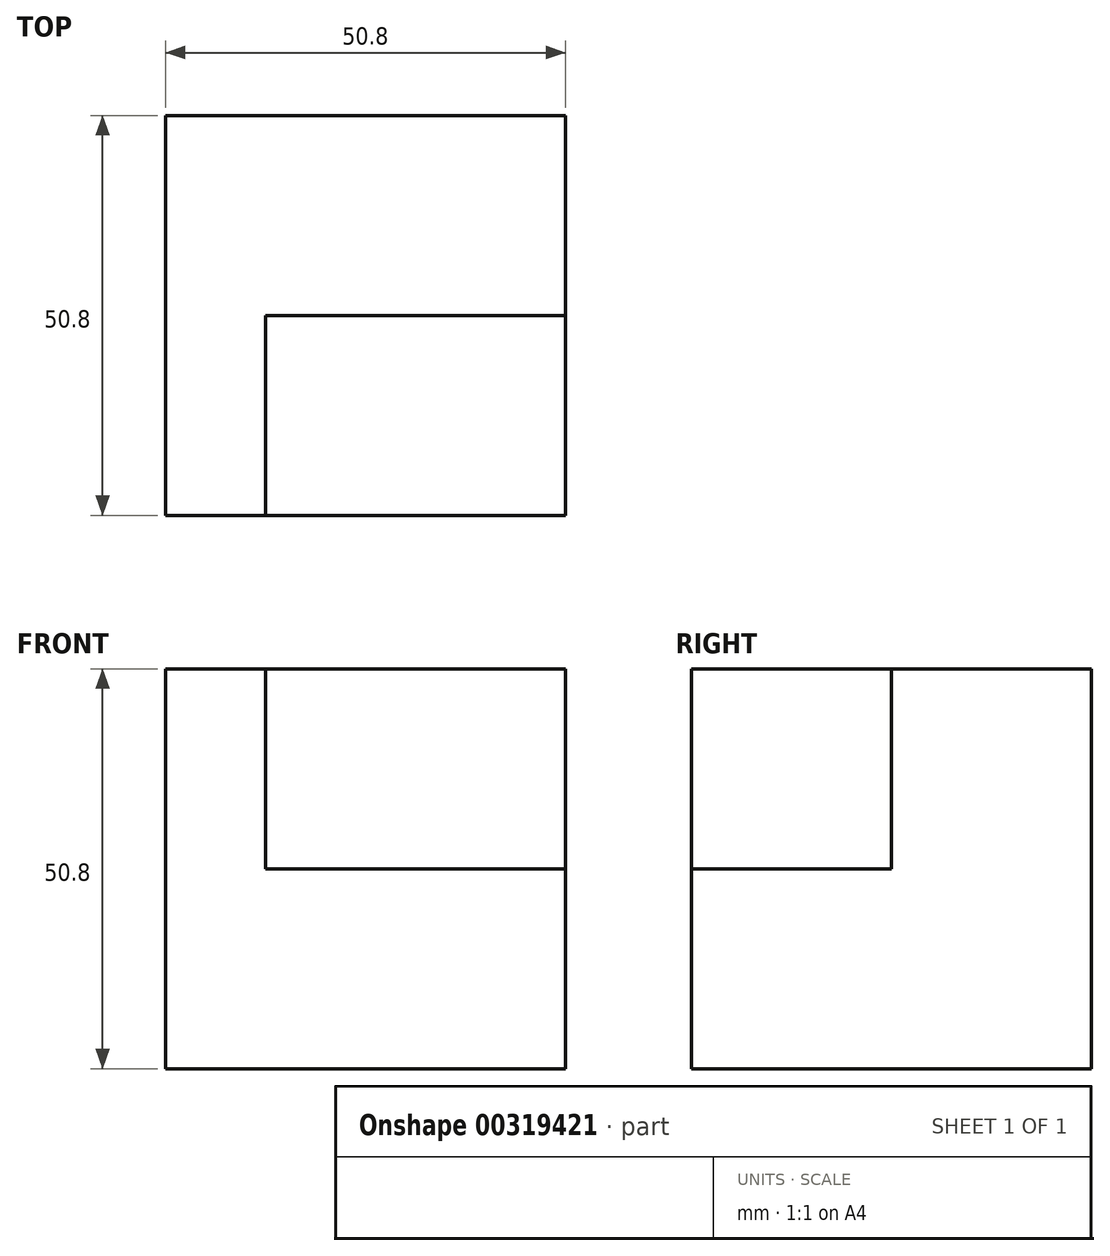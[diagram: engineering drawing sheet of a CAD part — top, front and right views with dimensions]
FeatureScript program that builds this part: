
annotation { "Feature Type Name" : "Feature", "Feature Type Description" : "" }
export const myFeature = defineFeature(function(context is Context, id is Id, definition is map)
    precondition{}
    {
        {
            var Q0;
            Q0=qCreatedBy(makeId("Top.planeOp"),FACE);
            var sketch = newSketch(context, id + "F0", { "sketchPlane" : qUnion([Q0])});
            skLineSegment(sketch, "E0", {"start": v(-38.83, -59.2) * mm, "end": v(11.97, -59.2) * mm});
            skLineSegment(sketch, "E1", {"start": v(11.97, -59.2) * mm, "end": v(11.97, -8.4) * mm});
            skLineSegment(sketch, "E2", {"start": v(11.97, -8.4) * mm, "end": v(-38.83, -8.4) * mm});
            skLineSegment(sketch, "E3", {"start": v(-38.83, -8.4) * mm, "end": v(-38.83, -59.2) * mm});
            skSolve(sketch);
        }
        {
            var Q0;
            Q0=makeQuery(id+"F0.imprint","IMPRINT",FACE,{"disambiguationData":[TD([[makeQuery(id+"F0.imprint","IMPRINT",EDGE,{"derivedFrom":sQuery(id+"F0.wireOp",EDGE,"E0")}),1.0]])]});
            extrude(context, id + "F1", {"entities" : qUnion([Q0]), "depth" : 25.4 * mm});
        }
        {
            var Q0;
            Q0=makeQuery(id+"F1.opExtrude","CAP_FACE",FACE,{"disambiguationData":[OSD([sQuery(id+"F0.wireOp",EDGE,"E0"),sQuery(id+"F0.wireOp",EDGE,"E1"),sQuery(id+"F0.wireOp",EDGE,"E2"),sQuery(id+"F0.wireOp",EDGE,"E3")])],"isStart":false});
            var sketch = newSketch(context, id + "F2", { "sketchPlane" : qUnion([Q0])});
            skLineSegment(sketch, "E4", {"start": v(-38.83, -59.2) * mm, "end": v(-26.13, -59.2) * mm});
            skLineSegment(sketch, "E5", {"start": v(-26.13, -59.2) * mm, "end": v(-26.13, -33.8) * mm});
            skLineSegment(sketch, "E6", {"start": v(-26.13, -33.8) * mm, "end": v(11.97, -33.8) * mm});
            skLineSegment(sketch, "E7", {"start": v(11.97, -33.8) * mm, "end": v(11.97, -8.4) * mm});
            skLineSegment(sketch, "E8", {"start": v(11.97, -8.4) * mm, "end": v(-38.83, -8.4) * mm});
            skLineSegment(sketch, "E9", {"start": v(-38.83, -8.4) * mm, "end": v(-38.83, -59.2) * mm});
            skSolve(sketch);
        }
        {
            var Q0;
            Q0=makeQuery(id+"F2.imprint","IMPRINT",FACE,{"disambiguationData":[TD([[makeQuery(id+"F2.imprint","IMPRINT",EDGE,{"derivedFrom":sQuery(id+"F2.wireOp",EDGE,"E4")}),1.0]])]});
            extrude(context, id + "F3", {"entities" : qUnion([Q0]), "operationType" : NewBodyOperationType.ADD, "depth" : 25.4 * mm});
        }
    });
